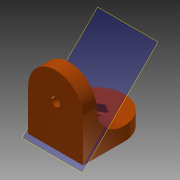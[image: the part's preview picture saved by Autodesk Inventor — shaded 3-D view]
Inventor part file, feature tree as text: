
AUTODESK INVENTOR PART (.ipt)
format: ipt  version: 2013 (Build 170138000, 138)  size: 142,848 bytes
history: native  units: mm
features: extrude x4, sketch x4, fillet x2, plane x1, mirror x1
ambient origin geometry x8: Origin, YZ Plane, XZ Plane, XY Plane, X Axis, Y Axis, Z Axis, Center Point
bodies: Solid1 (feature_tree)
feature tree (12):
  extrude  "Extrusion1"  Depth=25.0mm
  extrude  "Extrusion2"  Depth=5.0mm
  extrude  "Extrusion3"  Depth=3.1mm
  extrude  "Extrusion4"  Depth=5.6mm
  plane  "Work Plane1"
  mirror  "Mirror1"
  fillet  "Fillet1"  Radius=2.5mm
  fillet  "Fillet2"  Radius=10.0mm
  sketch  "Sketch1"  dims[d0=20.0mm d2=25.0mm]
  sketch  "Sketch2"  dims[d3=5.0mm d4=0.0mm d5=5.0mm]
  sketch  "Sketch3"  dims[d6=20.0mm d7=0.0mm d8=3.1mm]
  sketch  "Sketch4"  dims[d10=20.0mm d11=0.0mm d12=5.6mm d13=2.5mm d14=0.0mm d15=10.0mm d16=10.0mm]
